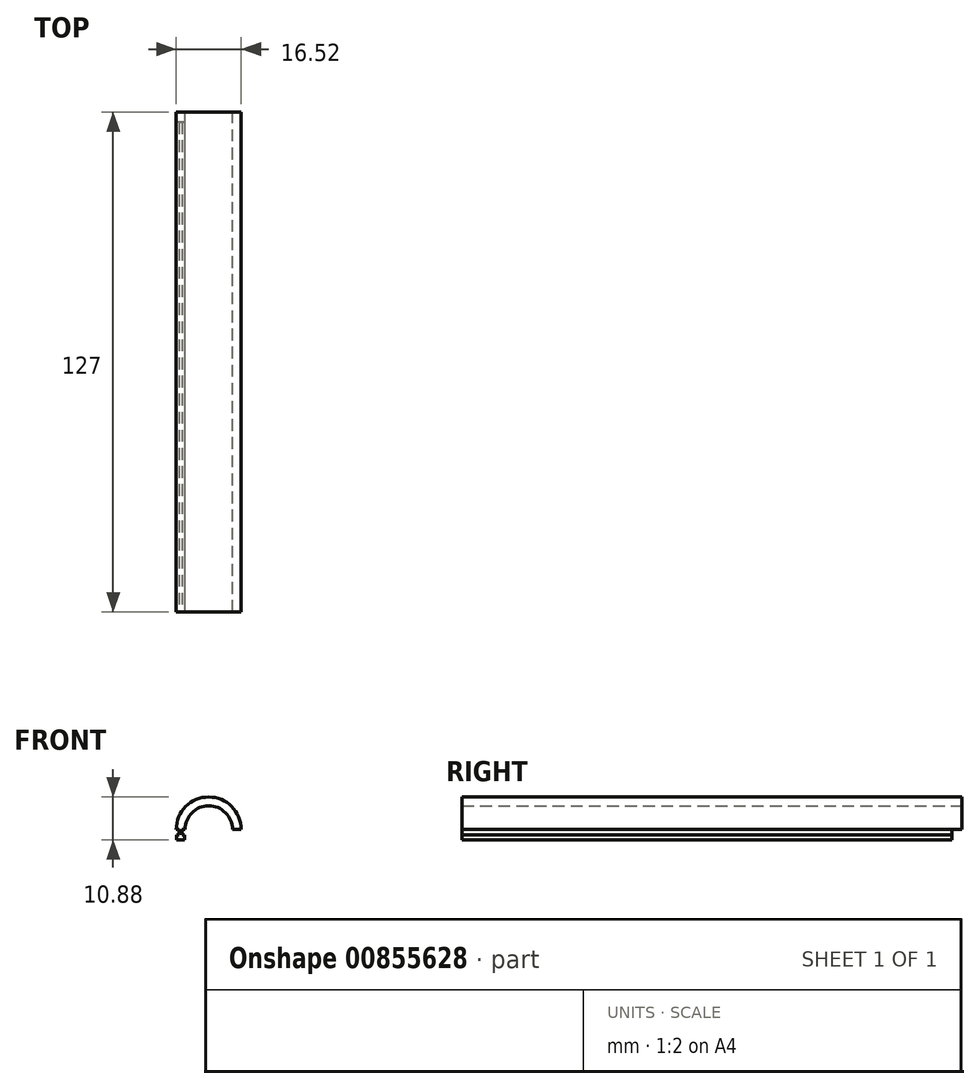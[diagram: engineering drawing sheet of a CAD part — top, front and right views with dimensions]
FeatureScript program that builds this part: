
annotation { "Feature Type Name" : "Feature", "Feature Type Description" : "" }
export const myFeature = defineFeature(function(context is Context, id is Id, definition is map)
    precondition{}
    {
        {
            var Q0;
            Q0=qCreatedBy(makeId("Front.planeOp"),FACE);
            var sketch = newSketch(context, id + "F0", { "sketchPlane" : qUnion([Q0])});
            skCircle(sketch, "E0", {"center": v(0, 0) * mm, "radius": 6.03 * mm});
            skLineSegment(sketch, "E1", {"start": v(-6.03, 0) * mm, "end": v(6.03, 0) * mm});
            skCircle(sketch, "E2", {"center": v(0, 0) * mm, "radius": 8.26 * mm});
            skLineSegment(sketch, "E3", {"start": v(-8.26, 0) * mm, "end": v(8.26, 0) * mm});
            skSolve(sketch);
        }
        {
            var Q0;
            {var subQ0=sQuery(id+"F0.wireOp",EDGE,"E3");var subQ5=sQuery(id+"F0.wireOp",EDGE,"E2");var subQ6=makeQuery(id+"F0.imprint","INTERSECT",VERTEX,{"disambiguationData":[OD(0.0)],"derivedFrom":[subQ5,subQ0]});Q0=makeQuery(id+"F0.imprint","IMPRINT",FACE,{"disambiguationData":[TD([[makeQuery(id+"F0.imprint","IMPRINT",EDGE,{"disambiguationData":[TD([[subQ6,-1.0]])],"derivedFrom":subQ5}),1.0]])]});}
            extrude(context, id + "F1", {"entities" : qUnion([Q0]), "endBound" : BoundingType.SYMMETRIC, "depth" : 127 * mm, "offsetDistance" : 25.4 * mm});
        }
        {
            var Q0;
            Q0=makeQuery(id+"F1.opExtrude","CAP_FACE",FACE,{"disambiguationData":[OSD([sQuery(id+"F0.wireOp",EDGE,"E0"),sQuery(id+"F0.wireOp",EDGE,"E2"),sQuery(id+"F0.wireOp",EDGE,"E3")])],"isStart":false});
            var sketch = newSketch(context, id + "F2", { "sketchPlane" : qUnion([Q0])});
            skLineSegment(sketch, "E4", {"start": v(-8.26, 0) * mm, "end": v(-7.5, 0) * mm});
            skLineSegment(sketch, "E5", {"start": v(-6.03, 0) * mm, "end": v(-6.8, 0) * mm});
            skLineSegment(sketch, "E6", {"start": v(-7.5, 0) * mm, "end": v(-7.5, -1.42) * mm});
            skLineSegment(sketch, "E7", {"start": v(-6.8, 0) * mm, "end": v(-6.8, -1.42) * mm});
            skLineSegment(sketch, "E8", {"start": v(-7.5, -1.42) * mm, "end": v(-8.13, -1.42) * mm});
            skLineSegment(sketch, "E9", {"start": v(-8.13, -1.42) * mm, "end": v(-8.13, -2.62) * mm});
            skLineSegment(sketch, "E10", {"start": v(-6.8, -1.42) * mm, "end": v(-6.16, -1.42) * mm});
            skLineSegment(sketch, "E11", {"start": v(-6.16, -1.42) * mm, "end": v(-6.16, -2.62) * mm});
            skLineSegment(sketch, "E12", {"start": v(-6.16, -2.62) * mm, "end": v(-8.13, -2.62) * mm});
            skSolve(sketch);
        }
        {
            var Q0;
            {var subQ1=sQuery(id+"F2.wireOp",EDGE,"E6");Q0=makeQuery(id+"F2.imprint","IMPRINT",FACE,{"disambiguationData":[TD([[makeQuery(id+"F2.imprint","IMPRINT",EDGE,{"derivedFrom":subQ1}),1.0]])]});}
            extrude(context, id + "F3", {"entities" : qUnion([Q0]), "operationType" : NewBodyOperationType.ADD, "oppositeDirection" : true, "depth" : 124.46 * mm, "offsetDistance" : 25.4 * mm});
        }
    });
